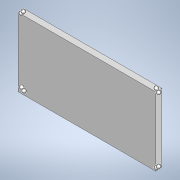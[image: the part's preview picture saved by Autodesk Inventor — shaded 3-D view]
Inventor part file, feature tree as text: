
AUTODESK INVENTOR PART (.ipt)
format: ipt  version: 2020.2 (Build 242310000, 310)  size: 147,456 bytes
history: native  units: in
note: dims shown in document units (in); Inventor stores cm internally (conversion verified against a paired STEP export)
features: sketch x3, extrude x2, hole x2
ambient origin geometry x8: Origin, YZ Plane, XZ Plane, XY Plane, X Axis, Y Axis, Z Axis, Center Point
bodies: Body1 (feature_tree)
feature tree (7):
  sketch  "Sketch1"  dims[d8=35.4331in d9=17.7165in]
  extrude  "Extrusion2"  Depth=17.7165in
  extrude  "Extrusion3"  Depth=1.5748in
  hole  "Hole1"  [1 undecoded]
  hole  "Hole2"  [1 undecoded]
  sketch  "Sketch2"  dims[d10=0.1181in d11=1.5748in]
  sketch  "Sketch3"  dims[d12=0.0in d13=0.1181in d14=0.0in d15=0.15in d16=0.2953in d17=0.1476in d18=0.0984in d19=90.0deg d20=0.3937in d21=0.8108in d22=0.5906in d23=0.5906in d24=0.5906in d25=0.5906in d26=0.5906in d27=0.5906in d28=0.5906in d29=0.5906in d30=0.15in d31=0.2953in d32=0.1476in d33=0.0984in d34=90.0deg d35=0.3937in d36=0.8108in d37=0.0in d38=0.0in d39=0.0in d40=0.0in d41=0.0in d42=0.0in d43=0.0in d44=0.0in]
note: 2 required parameter values undecoded (feature->parameter linkage not recoverable at this tier; creation-order binding heuristic only, values carry confidence <= 0.55)
